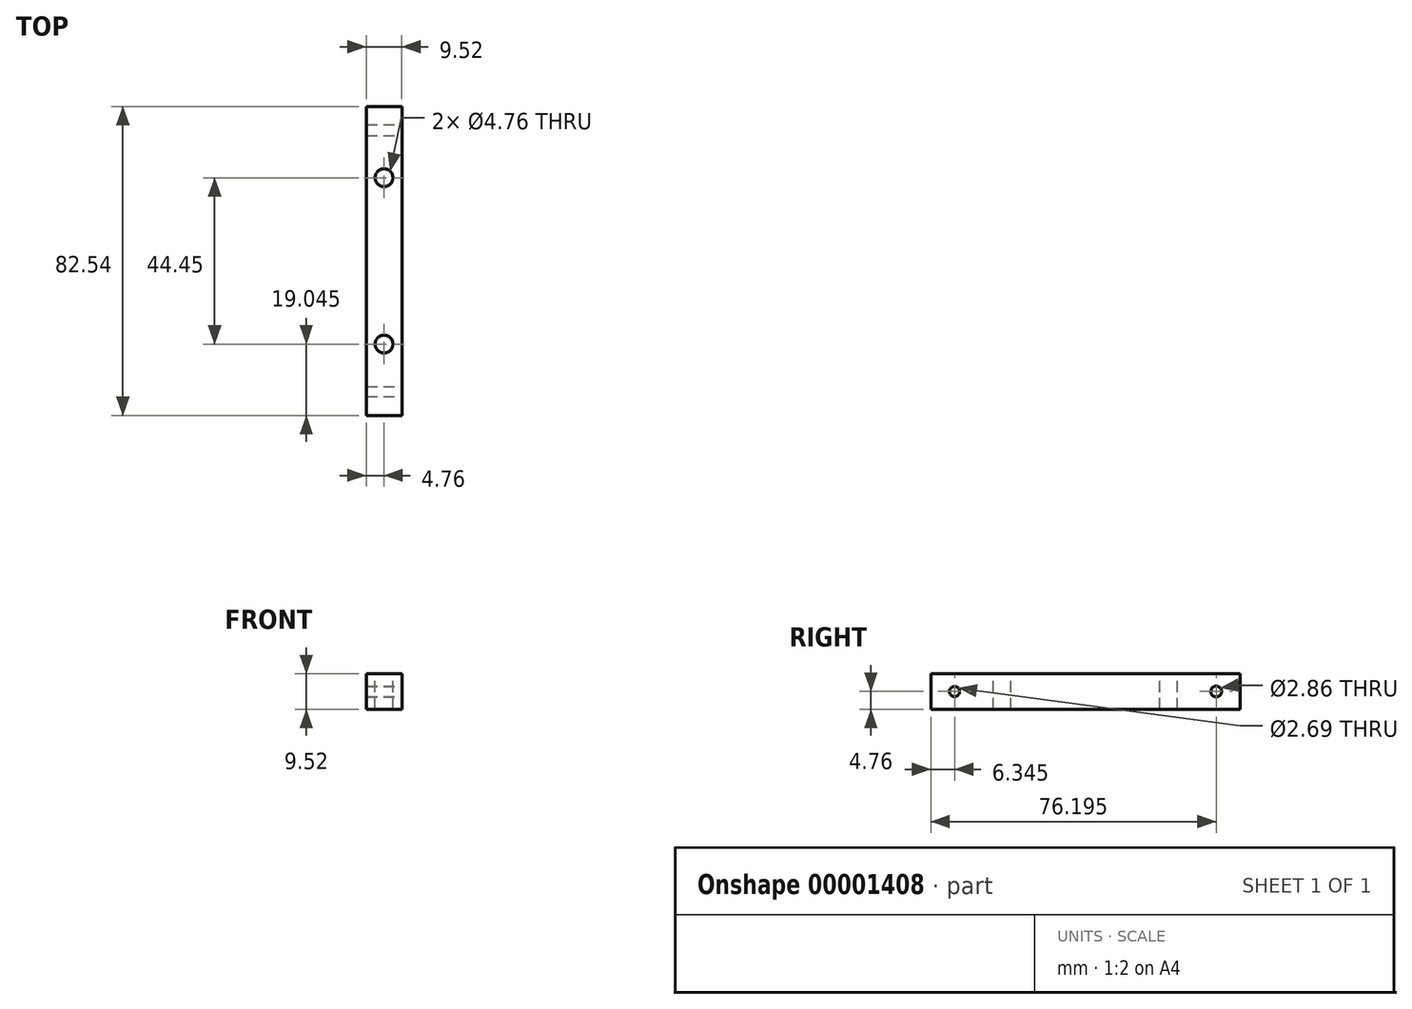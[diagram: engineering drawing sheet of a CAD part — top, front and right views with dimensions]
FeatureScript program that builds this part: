
annotation { "Feature Type Name" : "Feature", "Feature Type Description" : "" }
export const myFeature = defineFeature(function(context is Context, id is Id, definition is map)
    precondition{}
    {
        {
            var Q0;
            Q0=qCreatedBy(makeId("Front.planeOp"),FACE);
            var sketch = newSketch(context, id + "F0", { "sketchPlane" : qUnion([Q0])});
            skLineSegment(sketch, "E0.rect.bottom", {"start": v(4.76, 4.76) * mm, "end": v(-4.76, 4.76) * mm});
            skLineSegment(sketch, "E0.rect.top", {"start": v(4.76, -4.76) * mm, "end": v(-4.76, -4.76) * mm});
            skLineSegment(sketch, "E0.rect.left", {"start": v(4.76, 4.76) * mm, "end": v(4.76, -4.76) * mm});
            skLineSegment(sketch, "E0.rect.right", {"start": v(-4.76, 4.76) * mm, "end": v(-4.76, -4.76) * mm});
            skPoint(sketch, "E0.rect.middle", {"position": v(0, 0) * mm});
            skSolve(sketch);
        }
        {
            var Q0;
            Q0 = qSketchRegion(id + "F0", true);
            extrude(context, id + "F1", {"entities" : qUnion([Q0]), "endBound" : BoundingType.SYMMETRIC, "depth" : 82.55 * mm});
        }
        {
            var Q0;
            Q0=makeQuery(id+"F1.opExtrude","SWEPT_FACE",FACE,{"disambiguationData":[OSD([sQuery(id+"F0.wireOp",EDGE,"E0.rect.bottom")])]});
            var sketch = newSketch(context, id + "F2", { "sketchPlane" : qUnion([Q0])});
            skCircle(sketch, "E1", {"center": v(0, 22.23) * mm, "radius": 2.38 * mm});
            skCircle(sketch, "E2", {"center": v(0, -22.23) * mm, "radius": 2.38 * mm});
            skSolve(sketch);
        }
        {
            var Q0;
            Q0 = qSketchRegion(id + "F2", true);
            extrude(context, id + "F3", {"entities" : qUnion([Q0]), "operationType" : NewBodyOperationType.REMOVE, "endBound" : BoundingType.THROUGH_ALL, "oppositeDirection" : true, "depth" : 25.4 * mm});
        }
        {
            var Q0;
            Q0=makeQuery(id+"F1.opExtrude","SWEPT_FACE",FACE,{"disambiguationData":[OSD([sQuery(id+"F0.wireOp",EDGE,"E0.rect.left")])]});
            var sketch = newSketch(context, id + "F4", { "sketchPlane" : qUnion([Q0])});
            skCircle(sketch, "E3", {"center": v(-34.93, 0) * mm, "radius": 1.35 * mm});
            skCircle(sketch, "E4", {"center": v(34.93, 0) * mm, "radius": 1.43 * mm});
            skSolve(sketch);
        }
        {
            var Q0;
            Q0 = qSketchRegion(id + "F4", true);
            extrude(context, id + "F5", {"entities" : qUnion([Q0]), "operationType" : NewBodyOperationType.REMOVE, "endBound" : BoundingType.THROUGH_ALL, "oppositeDirection" : true, "depth" : 25.4 * mm});
        }
    });
